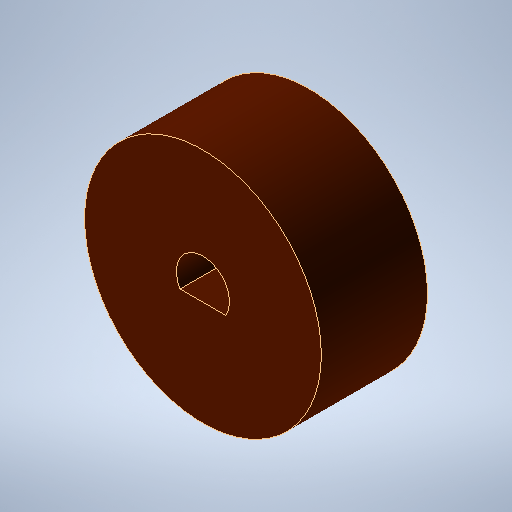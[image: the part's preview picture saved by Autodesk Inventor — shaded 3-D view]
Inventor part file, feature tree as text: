
AUTODESK INVENTOR PART (.ipt)
format: ipt  version: 2025.2 (Build 292293000, 293)  size: 493,568 bytes
history: native  units: mm
features: extrude x2, sketch x2, other x1
ambient origin geometry x8: Origin, YZ Plane, XZ Plane, XY Plane, X Axis, Y Axis, Z Axis, Center Point
bodies: Body1 (feature_tree)
feature tree (5):
  other  "Těleso1"
  extrude  "Vysunutí1"  Depth=29.0mm
  extrude  "Vysunutí2"  Depth=13.0mm TaperAngle=0.0deg
  sketch  "Náčrt1"
  sketch  "Náčrt2"
